# Revit family: 5c108e3a_0af5_4058_8456_616584e87cf6
name_source: partatom
category: Furniture
revit_build: Autodesk Revit 2015 (Build: 20140903_1530(x64)
units: mm (PartAtom-declared; Revit-internal decimal feet)

## types (1)
- Default
    BIMobject category = Other
    BIMobject category code = sanitary-sanitary-other
    BIMobject main category = Sanitary
    BIMobject main category code = sanitary
    BOSUseNativeGeometries = 1
    Brand url = http://www.hansgrohe-int.com
    Design country = Germany
    Edition number = 1
    GTIN code = https://4059625197042
    IFC Classification = Object
    Installation instructions = https://www.hansgrohe-usa.com
    Manufacturer country = Germany
    Manufacturer name = hansgrohe
    Product Guid = 651b48c4-59c0-4150-be66-6de4e2670fa7
    Product SKU = 04778830
    Product data url = https://bimobject.com
    Product family = Joleena
    Product group = Supplies
    Product name = 04778830 Joleena Baseplate 6"
    Product url = https://www.hansgrohe-usa.com
    QR code = http://bimobject.com
    Technical description = https://www.hansgrohe-usa.com

## geometry (parser evidence)
native form markers: Sweep x4
no freeform markers — native parametric forms only
